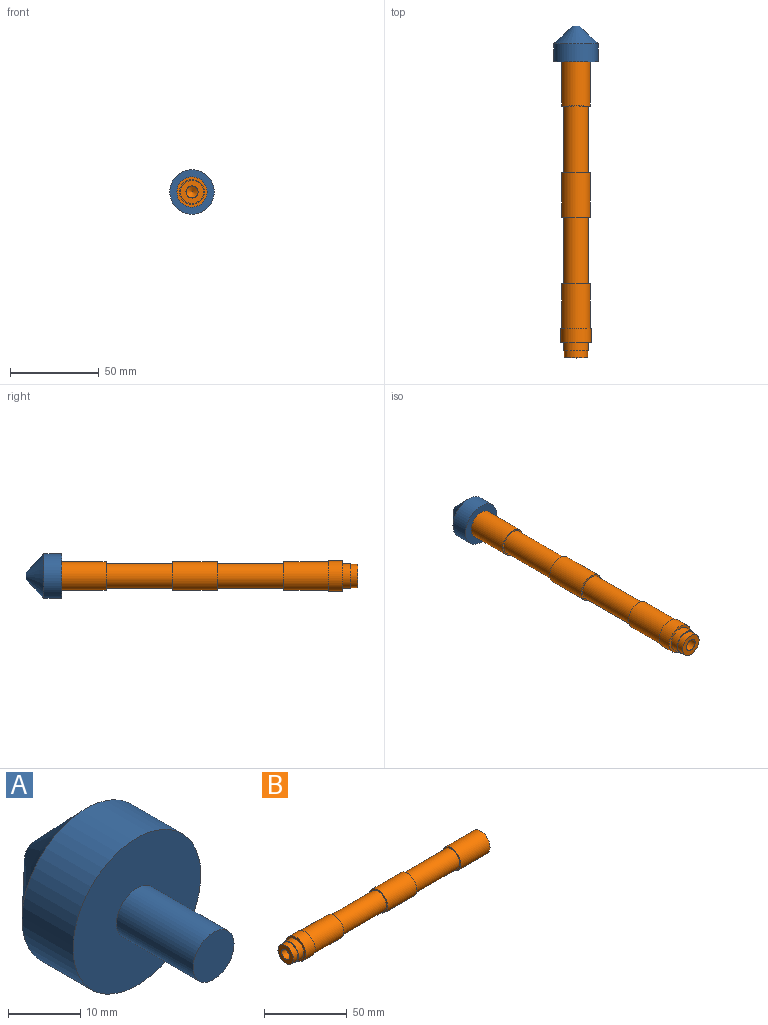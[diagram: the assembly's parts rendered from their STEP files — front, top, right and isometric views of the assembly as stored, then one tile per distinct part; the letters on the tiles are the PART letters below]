
ASSEMBLY  parts=2 mates=1
PART A: 6 faces, bbox 25x35x25 mm
  f0: plane 4x4mm, normal (0,1,0), area 12.6mm2, adj f1
  f1: cone r=2mm half-angle=46.4deg, axis (0,-1,0), area 660.5mm2, adj f0,f2
  f2: cylinder r=12.5mm len=25mm, axis (0,-1,0), area 785.4mm2, adj f1,f3
  f3: plane 25x25mm, normal (0,-1,0), area 440.6mm2, adj f2,f4
  f4: cylinder r=4mm len=15mm, axis (0,-1,0), area 377mm2, adj f3,f5
  f5: plane 8x8mm, normal (0,-1,0), area 50.3mm2, adj f4
PART B: 21 faces, bbox 166.7x17x17 mm
  f0: plane 13x13mm, normal (-1,0,0), area 96.4mm2, adj f16,f18
  f1: plane 16x16mm, normal (1,0,0), area 164.7mm2, adj f2,f20
  f2: cylinder r=8mm len=25mm, axis (-1,0,0), area 1256.6mm2, adj f1,f3
  f3: plane 16x16mm, normal (-1,0,0), area 47.1mm2, adj f2,f4
  f4: cylinder r=7mm len=37.5mm, axis (-1,0,0), area 1649.3mm2, adj f3,f5
  f5: plane 16x16mm, normal (1,0,0), area 47.1mm2, adj f4,f6
  f6: cylinder r=8mm len=25mm, axis (-1,0,0), area 1256.6mm2, adj f5,f7
  f7: plane 16x16mm, normal (-1,0,0), area 47.1mm2, adj f6,f8
  f8: cylinder r=7mm len=37.5mm, axis (-1,0,0), area 1649.3mm2, adj f7,f9
  f9: plane 16x16mm, normal (1,0,0), area 47.1mm2, adj f8,f10
  f10: cylinder r=8mm len=25mm, axis (-1,0,0), area 1256.6mm2, adj f9,f11
  f11: plane 17x17mm, normal (1,0,0), area 25.9mm2, adj f10,f12
  f12: cylinder r=8.5mm len=17mm, axis (-1,0,0), area 427.3mm2, adj f11,f13
  f13: plane 17x17mm, normal (-1,0,0), area 73mm2, adj f12,f14
  f14: cylinder r=7mm len=14mm, axis (-1,0,0), area 206.7mm2, adj f13,f15
  f15: plane 14x14mm, normal (-1,0,0), area 21.2mm2, adj f14,f16
  f16: cylinder r=6.5mm len=13mm, axis (-1,0,0), area 163.4mm2, adj f0,f15
  f17: cone r=0mm half-angle=59deg, axis (-1,0,0), area 42.4mm2, adj f18
  f18: cylinder r=3.4mm len=18.75mm, axis (-1,0,0), area 400.6mm2, adj f0,f17
  f19: cone r=0mm half-angle=59deg, axis (1,0,0), area 42.4mm2, adj f20
  f20: cylinder r=3.4mm len=18.75mm, axis (1,0,0), area 400.6mm2, adj f1,f19
PLACE A t=(-104.96,-20.72,8.41)mm
PLACE B rot(axis=(-0.58,-0.58,0.58),120deg) t=(-104.96,-189.41,8.41)mm
MATE fastened A.f1 <-> B.f2  axis (0,-1,0) through (-104.96,-20.72,8.41)mm
